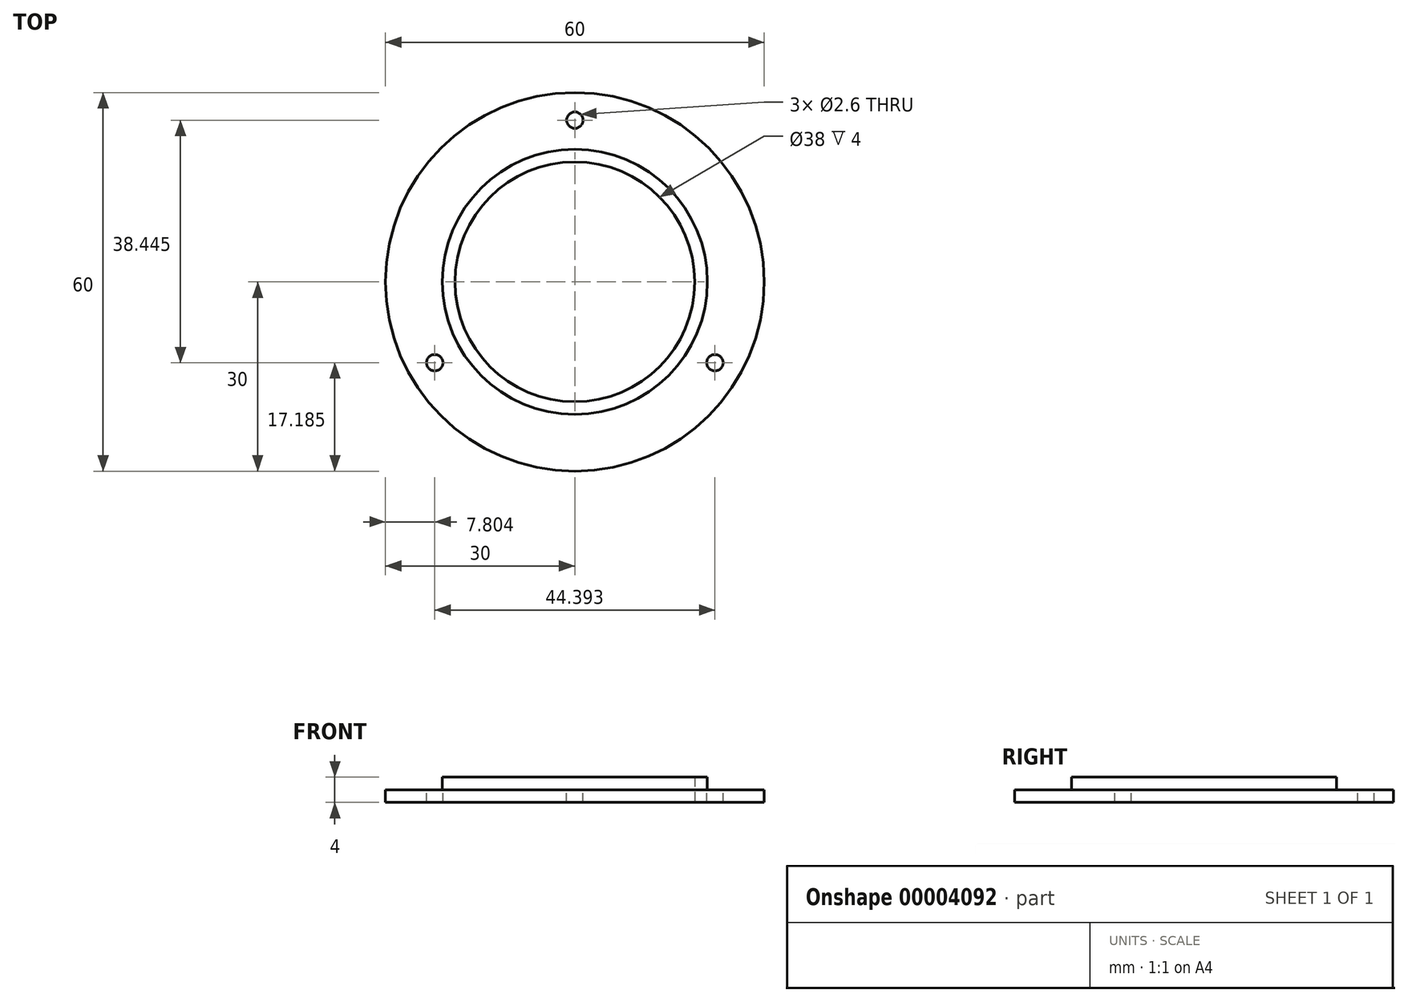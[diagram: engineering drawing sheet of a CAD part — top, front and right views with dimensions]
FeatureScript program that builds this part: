
annotation { "Feature Type Name" : "Feature", "Feature Type Description" : "" }
export const myFeature = defineFeature(function(context is Context, id is Id, definition is map)
    precondition{}
    {
        {
            var Q0;
            Q0=qCreatedBy(makeId("Top.planeOp"),FACE);
            var sketch = newSketch(context, id + "F0", { "sketchPlane" : qUnion([Q0])});
            skCircle(sketch, "E0", {"center": v(0, 0) * mm, "radius": 19 * mm});
            skCircle(sketch, "E1", {"center": v(0, 0) * mm, "radius": 30 * mm});
            skSolve(sketch);
        }
        {
            var Q0;
            Q0=makeQuery(id+"F0.imprint","IMPRINT",FACE,{"disambiguationData":[TD([[makeQuery(id+"F0.imprint","IMPRINT",EDGE,{"derivedFrom":sQuery(id+"F0.wireOp",EDGE,"E0")}),-1.0]])]});
            extrude(context, id + "F1", {"entities" : qUnion([Q0]), "depth" : 2 * mm});
        }
        {
            var Q0;
            Q0=makeQuery(id+"F1.opExtrude","CAP_FACE",FACE,{"disambiguationData":[OSD([sQuery(id+"F0.wireOp",EDGE,"E0"),sQuery(id+"F0.wireOp",EDGE,"E1")])],"isStart":false});
            var sketch = newSketch(context, id + "F2", { "sketchPlane" : qUnion([Q0])});
            skCircle(sketch, "E2", {"center": v(0, 0) * mm, "radius": 19 * mm});
            skCircle(sketch, "E3", {"center": v(0, 0) * mm, "radius": 21 * mm});
            skSolve(sketch);
        }
        {
            var Q0;
            Q0=makeQuery(id+"F2.imprint","IMPRINT",FACE,{"disambiguationData":[TD([[makeQuery(id+"F2.imprint","IMPRINT",EDGE,{"derivedFrom":sQuery(id+"F2.wireOp",EDGE,"E2")}),-1.0]])]});
            extrude(context, id + "F3", {"entities" : qUnion([Q0]), "operationType" : NewBodyOperationType.ADD, "depth" : 2 * mm});
        }
        {
            var Q0;
            Q0=makeQuery(id+"F1.opExtrude","CAP_FACE",FACE,{"disambiguationData":[OSD([sQuery(id+"F0.wireOp",EDGE,"E0"),sQuery(id+"F0.wireOp",EDGE,"E1")])],"isStart":false});
            var sketch = newSketch(context, id + "F4", { "sketchPlane" : qUnion([Q0])});
            skCircle(sketch, "E4", {"center": v(0, 25.63) * mm, "radius": 1.3 * mm});
            skCircle(sketch, "E5.1.0", {"center": v(-22.2, -12.82) * mm, "radius": 1.3 * mm});
            skCircle(sketch, "E5.2.0", {"center": v(22.2, -12.82) * mm, "radius": 1.3 * mm});
            skPoint(sketch, "E5.center", {"position": v(0, 0) * mm});
            skSolve(sketch);
        }
        {
            var Q0;
            Q0=makeQuery(id+"F4.imprint","IMPRINT",FACE,{"disambiguationData":[TD([[makeQuery(id+"F4.imprint","IMPRINT",EDGE,{"derivedFrom":sQuery(id+"F4.wireOp",EDGE,"E5.1.0")}),1.0]])]});
            var Q1;
            Q1=makeQuery(id+"F4.imprint","IMPRINT",FACE,{"disambiguationData":[TD([[makeQuery(id+"F4.imprint","IMPRINT",EDGE,{"derivedFrom":sQuery(id+"F4.wireOp",EDGE,"E4")}),1.0]])]});
            var Q2;
            Q2=makeQuery(id+"F4.imprint","IMPRINT",FACE,{"disambiguationData":[TD([[makeQuery(id+"F4.imprint","IMPRINT",EDGE,{"derivedFrom":sQuery(id+"F4.wireOp",EDGE,"E5.2.0")}),1.0]])]});
            var Q3;
            Q3=sQuery(id+"F4.wireOp",EDGE,"E4");
            var Q4;
            Q4=sQuery(id+"F4.wireOp",EDGE,"E5.1.0");
            var Q5;
            Q5=sQuery(id+"F4.wireOp",EDGE,"E5.2.0");
            extrude(context, id + "F5", {"entities" : qUnion([Q0, Q1, Q2]), "operationType" : NewBodyOperationType.REMOVE, "surfaceEntities" : qUnion([Q3, Q4, Q5]), "endBound" : BoundingType.THROUGH_ALL, "oppositeDirection" : true, "depth" : 25 * mm});
        }
    });
